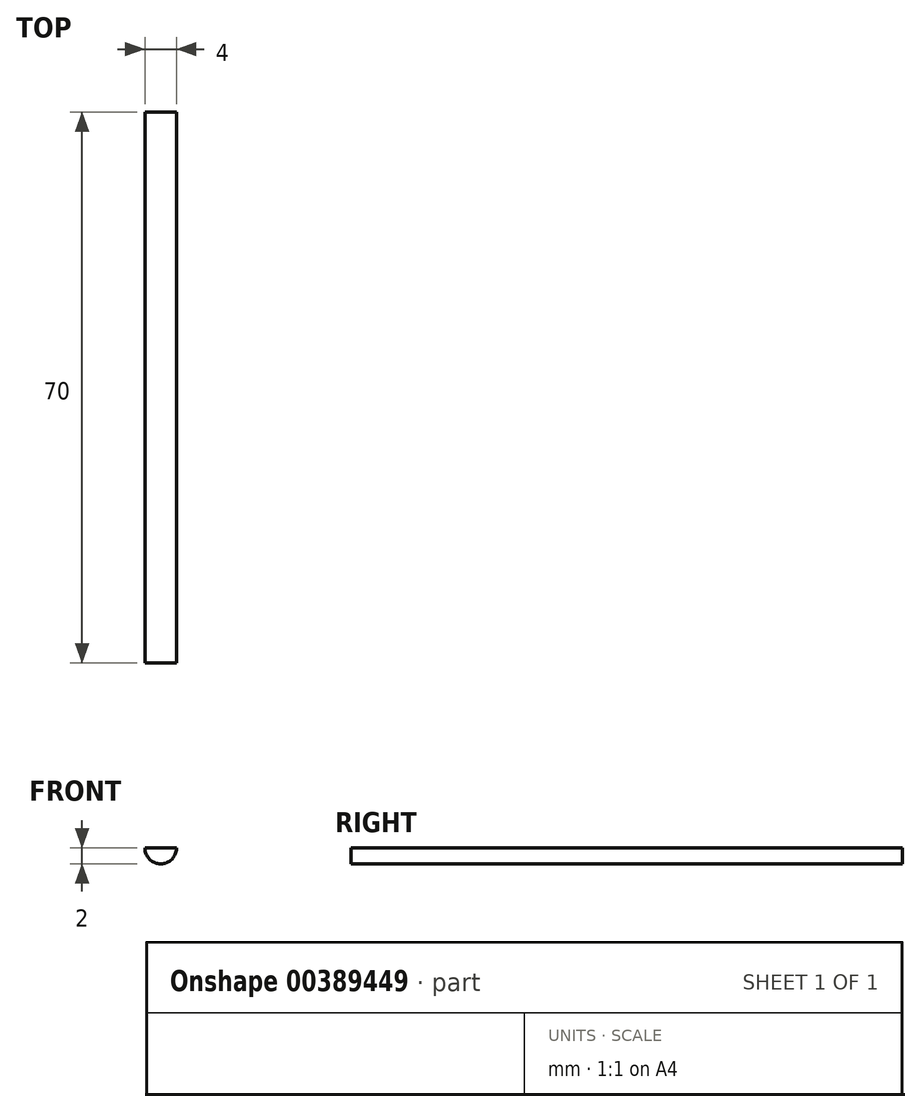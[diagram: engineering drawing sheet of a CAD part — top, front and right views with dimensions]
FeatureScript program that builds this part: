
annotation { "Feature Type Name" : "Feature", "Feature Type Description" : "" }
export const myFeature = defineFeature(function(context is Context, id is Id, definition is map)
    precondition{}
    {
        {
            var Q0;
            Q0=qCreatedBy(makeId("Front.planeOp"),FACE);
            var sketch = newSketch(context, id + "F0", { "sketchPlane" : qUnion([Q0])});
            skArc(sketch, "E0", {"start": v(-0.5, 1.94) * mm, "mid": v(0, -2) * mm, "end": v(0.5, 1.94) * mm});
            skLineSegment(sketch, "E1.bottom", {"start": v(0.5, 2.5) * mm, "end": v(-0.5, 2.5) * mm});
            skLineSegment(sketch, "E1.left", {"start": v(0.5, 2.5) * mm, "end": v(0.5, 1.94) * mm});
            skLineSegment(sketch, "E1.right", {"start": v(-0.5, 2.5) * mm, "end": v(-0.5, 1.94) * mm});
            skPoint(sketch, "E1.middle", {"position": v(0, 2) * mm});
            skPoint(sketch, "E2.orphan", {"position": v(-0.5, 1.5) * mm});
            skPoint(sketch, "E3.orphan", {"position": v(0.5, 1.5) * mm});
            skSolve(sketch);
        }
        {
            var Q0;
            Q0=qSketchRegion(id+"F0",true);
            var Q1;
            Q1=makeQuery(id+"F0.imprint","IMPRINT",FACE,{"disambiguationData":[TD([[makeQuery(id+"F0.imprint","IMPRINT",EDGE,{"derivedFrom":sQuery(id+"F0.wireOp",EDGE,"E0")}),1.0]])]});
            extrude(context, id + "F1", {"entities" : qUnion([Q0, Q1]), "depth" : 70 * mm});
        }
        {
            var Q0;
            Q0=makeQuery(id+"F1.opExtrude","CAP_FACE",FACE,{"disambiguationData":[OSD([sQuery(id+"F0.wireOp",EDGE,"E0"),sQuery(id+"F0.wireOp",EDGE,"E1.bottom"),sQuery(id+"F0.wireOp",EDGE,"E1.left"),sQuery(id+"F0.wireOp",EDGE,"E1.right")])],"isStart":false});
            cPlane(context, id + "F2", {"entities" : qUnion([Q0]), "cplaneType" : CPlaneType.OFFSET, "offset" : 10 * mm, "oppositeDirection" : true, "width" : 150 * mm, "height" : 150 * mm});
        }
        {
            var Q0;
            Q0=qCreatedBy(id+"F2.planeOp",FACE);
            var sketch = newSketch(context, id + "F3", { "sketchPlane" : qUnion([Q0])});
            skArc(sketch, "E4", {"start": v(0.5, 1.94) * mm, "mid": v(0, 2) * mm, "end": v(-0.5, 1.94) * mm});
            skLineSegment(sketch, "E5", {"start": v(-0.5, 2.5) * mm, "end": v(0.5, 2.5) * mm});
            skLineSegment(sketch, "E6", {"start": v(0.5, 1.94) * mm, "end": v(0.5, 2.5) * mm});
            skLineSegment(sketch, "E7", {"start": v(-0.5, 2.5) * mm, "end": v(-0.5, 1.94) * mm});
            skSolve(sketch);
        }
        {
            var Q0;
            Q0=makeQuery(id+"F3.imprint","IMPRINT",FACE,{"disambiguationData":[TD([[makeQuery(id+"F3.imprint","IMPRINT",EDGE,{"derivedFrom":sQuery(id+"F3.wireOp",EDGE,"E4")}),-1.0]])]});
            extrude(context, id + "F4", {"entities" : qUnion([Q0]), "operationType" : NewBodyOperationType.REMOVE, "oppositeDirection" : true, "depth" : 20 * mm});
        }
        {
            var Q0;
            Q0=makeQuery(id+"F1.opExtrude","CAP_FACE",FACE,{"disambiguationData":[OSD([sQuery(id+"F0.wireOp",EDGE,"E0"),sQuery(id+"F0.wireOp",EDGE,"E1.bottom"),sQuery(id+"F0.wireOp",EDGE,"E1.left"),sQuery(id+"F0.wireOp",EDGE,"E1.right")])],"isStart":true});
            var sketch = newSketch(context, id + "F5", { "sketchPlane" : qUnion([Q0])});
            skLineSegment(sketch, "E8", {"start": v(-0.5, 1.94) * mm, "end": v(-0.5, 2.5) * mm});
            skLineSegment(sketch, "E9", {"start": v(-0.5, 2.5) * mm, "end": v(0.5, 2.5) * mm});
            skLineSegment(sketch, "E10", {"start": v(0.5, 2.5) * mm, "end": v(0.5, 1.94) * mm});
            skArc(sketch, "E11", {"start": v(-0.5, 1.94) * mm, "mid": v(0, 2) * mm, "end": v(0.5, 1.94) * mm});
            skSolve(sketch);
        }
        {
            var Q0;
            Q0=makeQuery(id+"F5.imprint","IMPRINT",FACE,{"disambiguationData":[TD([[makeQuery(id+"F5.imprint","IMPRINT",EDGE,{"derivedFrom":sQuery(id+"F5.wireOp",EDGE,"E8")}),1.0]])]});
            extrude(context, id + "F6", {"entities" : qUnion([Q0]), "operationType" : NewBodyOperationType.REMOVE, "oppositeDirection" : true, "depth" : 15 * mm});
        }
        {
            var Q0;
            Q0=makeQuery(id+"F1.opExtrude","CAP_FACE",FACE,{"disambiguationData":[OSD([sQuery(id+"F0.wireOp",EDGE,"E0"),sQuery(id+"F0.wireOp",EDGE,"E1.bottom"),sQuery(id+"F0.wireOp",EDGE,"E1.left"),sQuery(id+"F0.wireOp",EDGE,"E1.right")])],"isStart":false});
            var sketch = newSketch(context, id + "F7", { "sketchPlane" : qUnion([Q0])});
            skLineSegment(sketch, "E12.bottom", {"start": v(2.59, 0) * mm, "end": v(-2.57, 0) * mm});
            skLineSegment(sketch, "E12.top", {"start": v(2.59, 3.25) * mm, "end": v(-2.57, 3.25) * mm});
            skLineSegment(sketch, "E12.left", {"start": v(2.59, 0) * mm, "end": v(2.59, 3.25) * mm});
            skLineSegment(sketch, "E12.right", {"start": v(-2.57, 0) * mm, "end": v(-2.57, 3.25) * mm});
            skSolve(sketch);
        }
        {
            var Q0;
            Q0=qSketchRegion(id+"F7",true);
            extrude(context, id + "F8", {"entities" : qUnion([Q0]), "operationType" : NewBodyOperationType.REMOVE, "oppositeDirection" : true, "depth" : 100 * mm});
        }
    });
